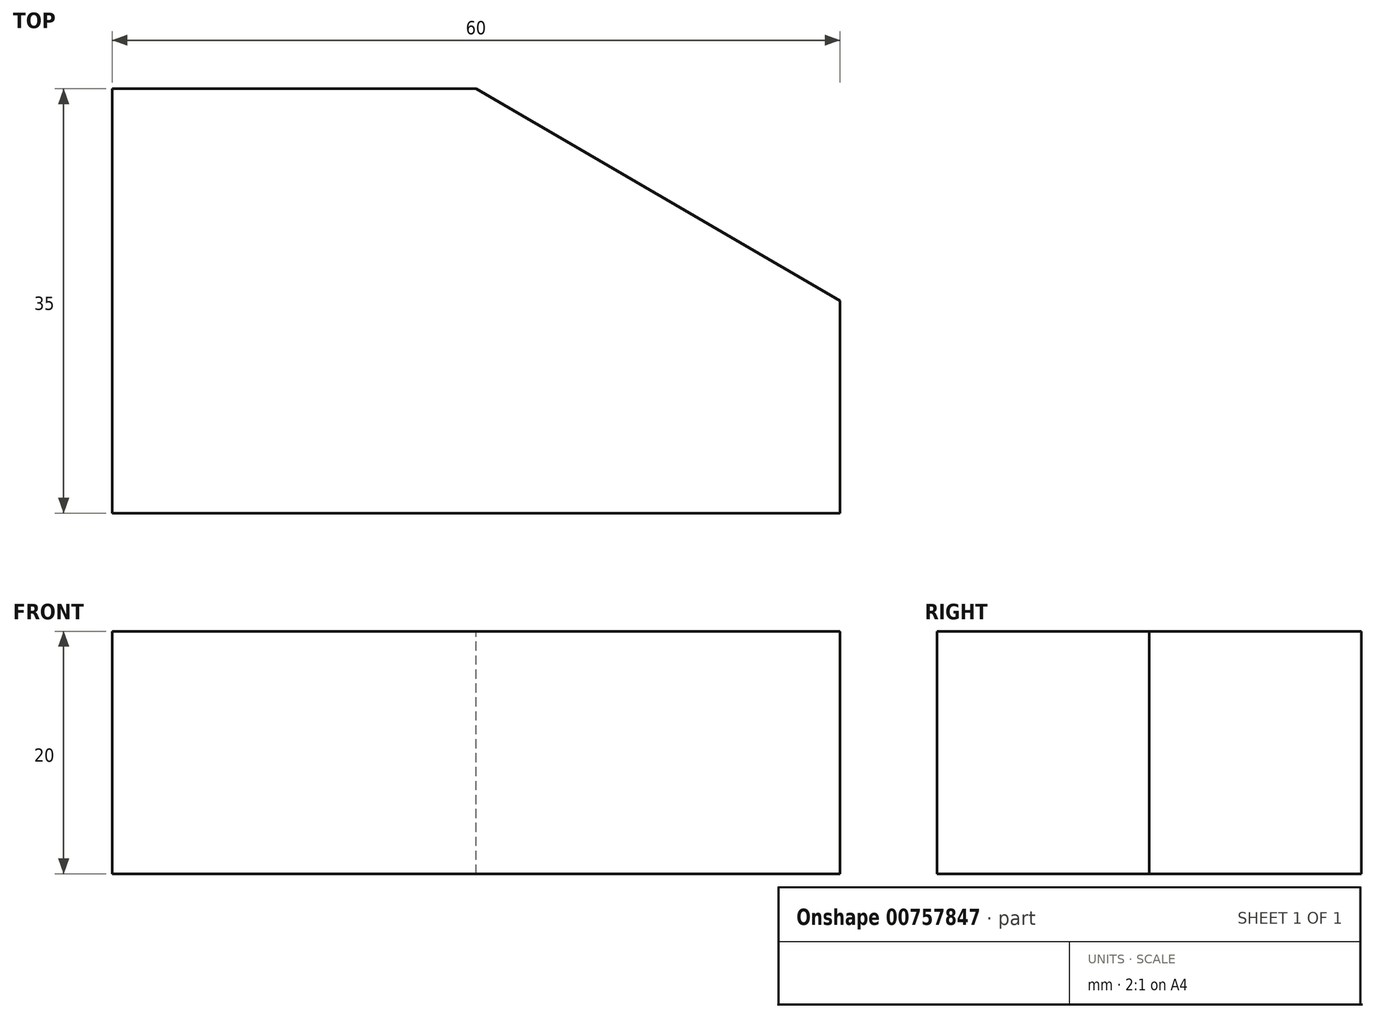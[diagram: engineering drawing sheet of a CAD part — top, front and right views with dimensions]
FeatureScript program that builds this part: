
annotation { "Feature Type Name" : "Feature", "Feature Type Description" : "" }
export const myFeature = defineFeature(function(context is Context, id is Id, definition is map)
    precondition{}
    {
        {
            var Q0;
            Q0=qCreatedBy(makeId("Top.planeOp"),FACE);
            var sketch = newSketch(context, id + "F0", { "sketchPlane" : qUnion([Q0])});
            skLineSegment(sketch, "E0", {"start": v(0, 0) * mm, "end": v(60, 0) * mm});
            skLineSegment(sketch, "E1", {"start": v(60, 0) * mm, "end": v(60, 35) * mm});
            skLineSegment(sketch, "E2", {"start": v(60, 35) * mm, "end": v(0, 35) * mm});
            skLineSegment(sketch, "E3", {"start": v(0, 35) * mm, "end": v(0, 0) * mm});
            skSolve(sketch);
        }
        {
            var Q0;
            Q0 = qSketchRegion(id + "F0", true);
            extrude(context, id + "F1", {"entities" : qUnion([Q0]), "depth" : 20 * mm, "offsetDistance" : 25 * mm});
        }
        {
            var Q0;
            Q0=makeQuery(id+"F1.opExtrude","CAP_FACE",FACE,{"disambiguationData":[OSD([sQuery(id+"F0.wireOp",EDGE,"E0"),sQuery(id+"F0.wireOp",EDGE,"E1"),sQuery(id+"F0.wireOp",EDGE,"E2"),sQuery(id+"F0.wireOp",EDGE,"E3")])],"isStart":false});
            var sketch = newSketch(context, id + "F2", { "sketchPlane" : qUnion([Q0])});
            skLineSegment(sketch, "E4", {"start": v(30, 35) * mm, "end": v(60, 17.5) * mm});
            skSolve(sketch);
        }
        {
            var Q0;
            {var subQ0=sQuery(id+"F2.wireOp",EDGE,"E4");Q0=makeQuery(id+"F2.imprint","IMPRINT",FACE,{"disambiguationData":[TD([[makeQuery(id+"F2.imprint","IMPRINT",EDGE,{"derivedFrom":subQ0}),1.0]])]});}
            extrude(context, id + "F3", {"entities" : qUnion([Q0]), "operationType" : NewBodyOperationType.REMOVE, "endBound" : BoundingType.THROUGH_ALL, "oppositeDirection" : true, "depth" : 25 * mm, "offsetDistance" : 25 * mm});
        }
    });
